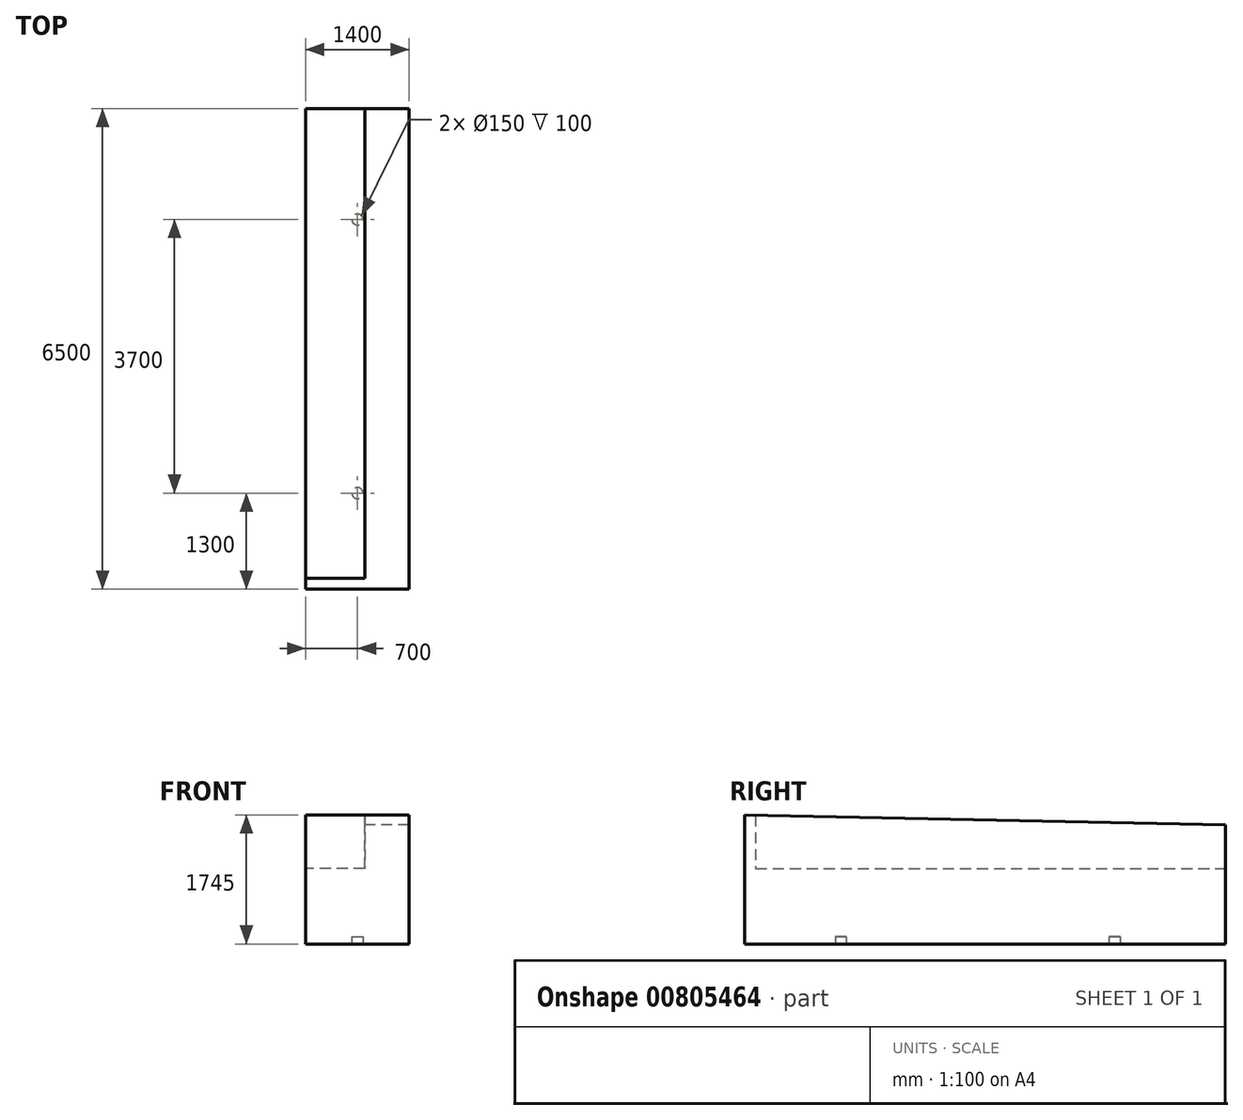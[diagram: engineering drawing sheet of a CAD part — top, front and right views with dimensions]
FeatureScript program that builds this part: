
annotation { "Feature Type Name" : "Feature", "Feature Type Description" : "" }
export const myFeature = defineFeature(function(context is Context, id is Id, definition is map)
    precondition{}
    {
        {
            var Q0;
            Q0=qCreatedBy(makeId("Right.planeOp"),FACE);
            var sketch = newSketch(context, id + "F0", { "sketchPlane" : qUnion([Q0])});
            skLineSegment(sketch, "E0", {"start": v(0, 0) * mm, "end": v(6500, 0) * mm});
            skLineSegment(sketch, "E1", {"start": v(6500, 0) * mm, "end": v(6500, 1610) * mm});
            skLineSegment(sketch, "E2", {"start": v(6500, 1610) * mm, "end": v(0, 1745) * mm});
            skLineSegment(sketch, "E3", {"start": v(0, 1745) * mm, "end": v(0, 0) * mm});
            skSolve(sketch);
        }
        {
            var Q0;
            Q0 = qSketchRegion(id + "F0", true);
            extrude(context, id + "F1", {"entities" : qUnion([Q0]), "depth" : 1400 * mm, "offsetDistance" : 25 * mm});
        }
        {
            var Q0;
            Q0=qCreatedBy(makeId("Right.planeOp"),FACE);
            var sketch = newSketch(context, id + "F2", { "sketchPlane" : qUnion([Q0])});
            skLineSegment(sketch, "E4", {"start": v(6500, 1022) * mm, "end": v(6500, 1610) * mm});
            skLineSegment(sketch, "E5", {"start": v(6500, 1610) * mm, "end": v(150, 1741.88) * mm});
            skLineSegment(sketch, "E6", {"start": v(150, 1741.88) * mm, "end": v(150, 1022) * mm});
            skLineSegment(sketch, "E7", {"start": v(150, 1022) * mm, "end": v(6500, 1022) * mm});
            skSolve(sketch);
        }
        {
            var Q0;
            Q0 = qSketchRegion(id + "F2", true);
            extrude(context, id + "F3", {"entities" : qUnion([Q0]), "operationType" : NewBodyOperationType.REMOVE, "depth" : 800 * mm, "offsetDistance" : 25 * mm});
        }
        {
            var Q0;
            Q0=makeQuery(id+"F1.opExtrude","SWEPT_FACE",FACE,{"disambiguationData":[OSD([sQuery(id+"F0.wireOp",EDGE,"E0")])]});
            var sketch = newSketch(context, id + "F4", { "sketchPlane" : qUnion([Q0])});
            skCircle(sketch, "E8", {"center": v(700, -1300) * mm, "radius": 75 * mm});
            skCircle(sketch, "E9", {"center": v(700, -5000) * mm, "radius": 75 * mm});
            skSolve(sketch);
        }
        {
            var Q0;
            Q0 = qSketchRegion(id + "F4", true);
            extrude(context, id + "F5", {"entities" : qUnion([Q0]), "operationType" : NewBodyOperationType.REMOVE, "oppositeDirection" : true, "depth" : 100 * mm, "offsetDistance" : 25 * mm});
        }
    });
